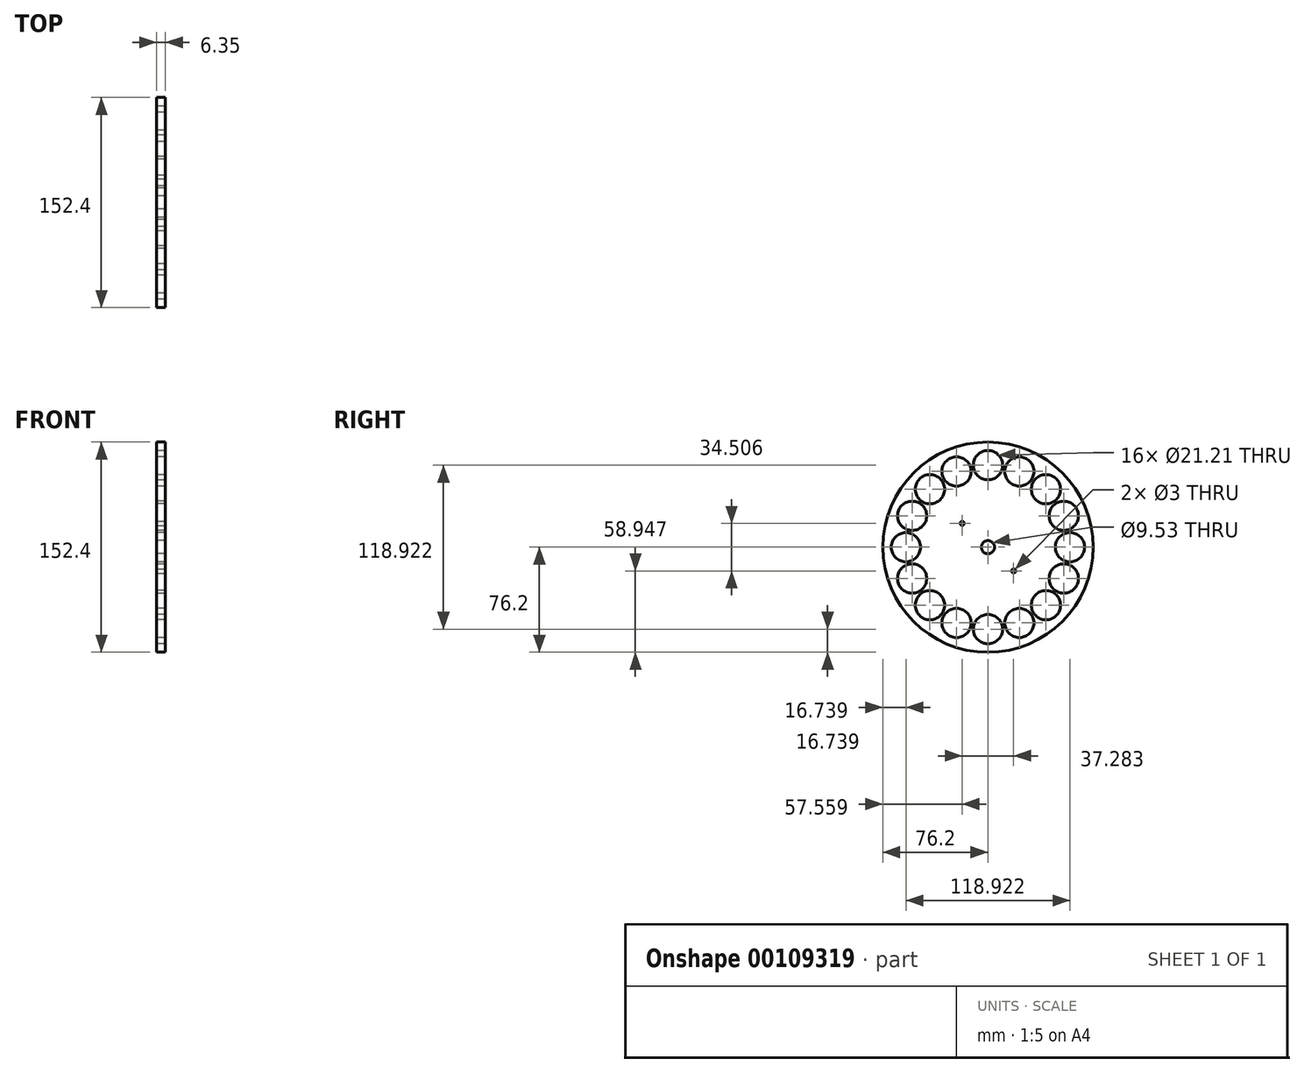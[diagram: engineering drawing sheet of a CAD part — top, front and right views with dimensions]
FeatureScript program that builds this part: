
annotation { "Feature Type Name" : "Feature", "Feature Type Description" : "" }
export const myFeature = defineFeature(function(context is Context, id is Id, definition is map)
    precondition{}
    {
        {
            var Q0;
            Q0=qCreatedBy(makeId("Right.planeOp"),FACE);
            var sketch = newSketch(context, id + "F0", { "sketchPlane" : qUnion([Q0])});
            skCircle(sketch, "E0", {"center": v(0, 0) * mm, "radius": 76.2 * mm});
            skCircle(sketch, "E1", {"center": v(0, 0) * mm, "radius": 1.46 * mm});
            skLineSegment(sketch, "E2", {"start": v(0, 0) * mm, "end": v(0, 76.2) * mm, "construction": true});
            skLineSegment(sketch, "E3", {"start": v(0, 76.2) * mm, "end": v(-76.2, 0) * mm, "construction": true});
            skLineSegment(sketch, "E4", {"start": v(-76.2, 0) * mm, "end": v(0, 0) * mm, "construction": true});
            skLineSegment(sketch, "E5", {"start": v(0, 0) * mm, "end": v(0, -76.2) * mm, "construction": true});
            skLineSegment(sketch, "E6", {"start": v(0, -76.2) * mm, "end": v(-76.2, 0) * mm, "construction": true});
            skLineSegment(sketch, "E7", {"start": v(0, 0) * mm, "end": v(76.2, 0) * mm, "construction": true});
            skLineSegment(sketch, "E8", {"start": v(76.2, 0) * mm, "end": v(0, -76.2) * mm, "construction": true});
            skLineSegment(sketch, "E9", {"start": v(76.2, 0) * mm, "end": v(0, 76.2) * mm, "construction": true});
            skLineSegment(sketch, "E10", {"start": v(-38.1, 38.1) * mm, "end": v(38.1, -38.1) * mm, "construction": true});
            skLineSegment(sketch, "E11", {"start": v(-38.1, -38.1) * mm, "end": v(38.1, 38.1) * mm, "construction": true});
            skLineSegment(sketch, "E12", {"start": v(38.1, 38.1) * mm, "end": v(53.88, 53.88) * mm, "construction": true});
            skLineSegment(sketch, "E13", {"start": v(-38.1, -38.1) * mm, "end": v(-53.88, -53.88) * mm, "construction": true});
            skLineSegment(sketch, "E14", {"start": v(38.1, -38.1) * mm, "end": v(53.88, -53.88) * mm, "construction": true});
            skLineSegment(sketch, "E15", {"start": v(-38.1, 38.1) * mm, "end": v(-53.88, 53.88) * mm, "construction": true});
            skLineSegment(sketch, "E16", {"start": v(-46, 46) * mm, "end": v(-38.1, 38.1) * mm});
            skCircle(sketch, "E17", {"center": v(-42.05, 42.05) * mm, "radius": 10.6 * mm});
            skCircle(sketch, "E18", {"center": v(0, 0) * mm, "radius": 4.76 * mm});
            skSolve(sketch);
        }
        {
            var Q0;
            Q0=makeQuery(id+"F0.imprint","IMPRINT",FACE,{"disambiguationData":[TD([[makeQuery(id+"F0.imprint","IMPRINT",EDGE,{"derivedFrom":sQuery(id+"F0.wireOp",EDGE,"E0")}),1.0]])]});
            extrude(context, id + "F1", {"entities" : qUnion([Q0]), "depth" : 6.35 * mm});
        }
        {
            var Q0;
            Q0=makeQuery(id+"F0.imprint","IMPRINT",FACE,{"disambiguationData":[TD([[makeQuery(id+"F0.imprint","IMPRINT",EDGE,{"derivedFrom":sQuery(id+"F0.wireOp",EDGE,"E17")}),1.0]])]});
            extrude(context, id + "F2", {"entities" : qUnion([Q0]), "depth" : 25.4 * mm});
        }
        {
            var Q0;
            Q0=makeQuery(id+"F2.opExtrude","SWEPT_BODY",BODY,{"disambiguationData":[OSD([sQuery(id+"F0.wireOp",EDGE,"E17")])]});
            var Q1;
            Q1=sQuery(id+"F0.wireOp",EDGE,"E0");
            circularPattern(context, id + "F3", {"operationType" : NewBodyOperationType.REMOVE, "entities" : qUnion([Q0]), "axis" : qUnion([Q1]), "angle" : 360 * degree, "instanceCount" : 16, "equalSpace" : true});
        }
        {
            var Q0;
            Q0=makeQuery(id+"F1.opExtrude","CAP_FACE",FACE,{"disambiguationData":[OSD([sQuery(id+"F0.wireOp",EDGE,"E0"),sQuery(id+"F0.wireOp",EDGE,"E1"),sQuery(id+"F0.wireOp",EDGE,"E17")])],"isStart":false});
            var sketch = newSketch(context, id + "F4", { "sketchPlane" : qUnion([Q0])});
            skLineSegment(sketch, "E19", {"start": v(55.92, -51.76) * mm, "end": v(0, 0) * mm, "construction": true});
            skLineSegment(sketch, "E20", {"start": v(0, 0) * mm, "end": v(-55.92, 51.76) * mm, "construction": true});
            skLineSegment(sketch, "E21", {"start": v(0, 0) * mm, "end": v(51.76, 55.92) * mm, "construction": true});
            skLineSegment(sketch, "E22", {"start": v(0, 0) * mm, "end": v(-51.76, -55.92) * mm, "construction": true});
            skCircle(sketch, "E23", {"center": v(-18.64, 17.25) * mm, "radius": 1.5 * mm});
            skCircle(sketch, "E24", {"center": v(18.64, -17.25) * mm, "radius": 1.5 * mm});
            skSolve(sketch);
        }
        {
            var Q0;
            Q0 = qSketchRegion(id + "F4", true);
            extrude(context, id + "F5", {"entities" : qUnion([Q0]), "operationType" : NewBodyOperationType.REMOVE, "oppositeDirection" : true, "depth" : 25.4 * mm});
        }
    });
